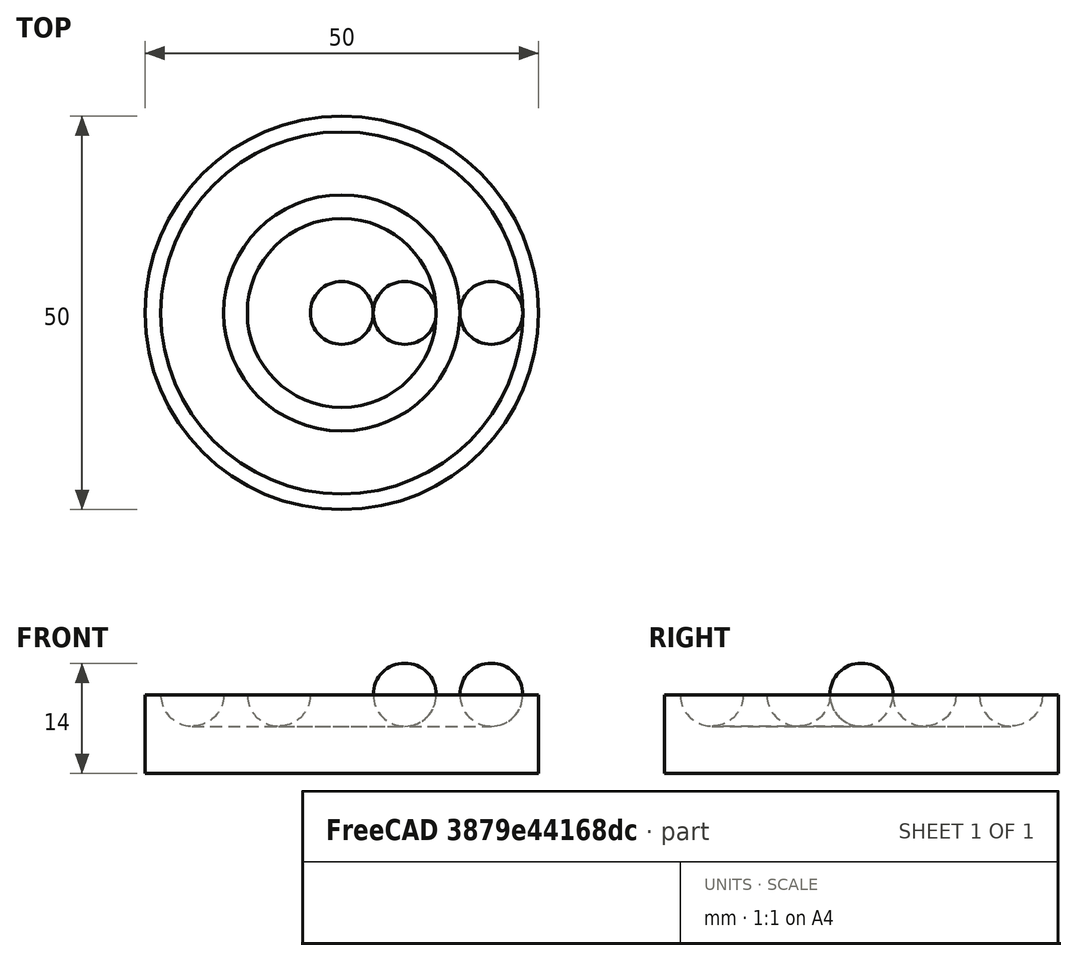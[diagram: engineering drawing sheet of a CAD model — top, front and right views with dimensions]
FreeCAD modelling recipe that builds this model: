
FCSTD DOCUMENT  (FreeCAD 1.0R39319 (Git))
Label: ojt1_t15r02_toolholders
License: All rights reserved
LicenseURL: https://en.wikipedia.org/wiki/All_rights_reserved
objects: Part::Torus×2, Part::Cut×2, Part::Sphere×2, Part::Cylinder×1
note: 7 computed .brp shape members not serialized (recipe doc carries the construction recipe); baked Part::Feature solids carry a one-line shape summary decoded from their .brp

FEATURE [Part::Cylinder] Cylinder  label="Cilindre"
  Angle = 360
  AttacherType = Attacher::AttachEngine3D
  FirstAngle = 0
  Height = 10
  Radius = 25
  SecondAngle = 0
FEATURE [Part::Torus] Torus
  Angle1 = -180
  Angle2 = 180
  Angle3 = 360
  AttacherType = Attacher::AttachEngine3D
  Placement = pos=(0,0,10) rot=(0,0,1;0rad)
  Radius1 = 19
  Radius2 = 4
FEATURE [Part::Torus] Torus001
  Angle1 = -180
  Angle2 = 180
  Angle3 = 360
  AttacherType = Attacher::AttachEngine3D
  Placement = pos=(0,0,10) rot=(0,0,1;0rad)
  Radius1 = 8
  Radius2 = 4
FEATURE [Part::Cut] Cut
  Base = -> Cylinder
  Refine = true
  Tool = -> Torus
FEATURE [Part::Cut] Cut001
  Base = -> Cut
  Refine = true
  Tool = -> Torus001
FEATURE [Part::Sphere] Sphere  label="Esfera"
  Angle1 = -90
  Angle2 = 90
  Angle3 = 360
  AttacherType = Attacher::AttachEngine3D
  Placement = pos=(8,0,10) rot=(0,0,1;0rad)
  Radius = 4
FEATURE [Part::Sphere] Sphere001  label="Esfera001"
  Angle1 = -90
  Angle2 = 90
  Angle3 = 360
  AttacherType = Attacher::AttachEngine3D
  Placement = pos=(19,0,10) rot=(0,0,1;0rad)
  Radius = 4
